# Revit family: Переходник с наружной резьбой
name_source: partatom
category: Соединительные детали трубопроводов
revit_build: Autodesk Revit 2017 (Build: 20160225_1515(x64)
units: mm (PartAtom-declared; Revit-internal decimal feet)

## family parameters
Всегда вертикально = Да
На основе рабочей плоскости = Нет
Общий = Нет
При загрузке вырезать с полостями = Нет
Размер круглого соединителя = Использовать радиус
Тип детали = Соединение

## types (12) — shared parameters
ADSK_Единица измерения = шт
ADSK_Завод-изготовитель = Sanext
URL = http://sanext.ru
Изготовитель = Sanext
Материал фитинга = DZR латунь
Разработчик = ООО ПРОРУБИМ
Разработчик (телефон) = +7(495)649-85-43
Разработчик модели (URL) = http://prorubim.com
zero-valued in all types: ADSK_Масса

## per-type parameters (varying)
| type | ADSK_Код изделия | D1 | DN | G | G/2 | G1/2 | R | R1 | S | a | Лево | Право |
| Переходник с наружной резьбой  63xR 2" | 4275 | 68 мм | 63 мм | 63 мм | 32 мм | 33 мм | 32 мм | 29 мм | 68 мм | 106 мм | Нет | Да |
| Переходник с наружной резьбой  50xR1 1/4" | 4263 | 55 мм | 50 мм | 40 мм | 20 мм | 27 мм | 25 мм | 22 мм | 55 мм | 90 мм | Да | Нет |
| Переходник с наружной резьбой  40xR1 1/4" | 4253 | 45 мм | 40 мм | 40 мм | 20 мм | 22 мм | 20 мм | 17 мм | 45 мм | 83 мм | Нет | Да |
| Переходник с наружной резьбой  32xR1" | 4242 | 37 мм | 32 мм | 32 мм | 16 мм | 18 мм | 16 мм | 13 мм | 37 мм | 73 мм | Нет | Да |
| Переходник с наружной резьбой  32xR3/4" | 4241 | 37 мм | 32 мм | 25 мм | 13 мм | 18 мм | 16 мм | 13 мм | 37 мм | 69 мм | Да | Нет |
| Переходник с наружной резьбой  25xR1" | 4232 | 37 мм | 25 мм | 32 мм | 16 мм | 18 мм | 13 мм | 10 мм | 37 мм | 69 мм | Нет | Да |
| Переходник с наружной резьбой  25xR3/4" | 4231 | 30 мм | 25 мм | 25 мм | 13 мм | 14 мм | 13 мм | 10 мм | 30 мм | 68 мм | Нет | Да |
| Переходник с наружной резьбой  20xR3/4" | 4221 | 30 мм | 20 мм | 25 мм | 13 мм | 14 мм | 10 мм | 7 мм | 30 мм | 56 мм | Нет | Да |
| Переходник с наружной резьбой  20xR1/2" | 4220 | 25 мм | 20 мм | 20 мм | 10 мм | 12 мм | 10 мм | 7 мм | 25 мм | 56 мм | Нет | Да |
| Переходник с наружной резьбой  16xR3/4" | 4211 | 30 мм | 16 мм | 25 мм | 13 мм | 14 мм | 8 мм | 5 мм | 30 мм | 50 мм | Нет | Да |
| Переходник с наружной резьбой  16xR1/2" | 4210 | 25 мм | 16 мм | 20 мм | 10 мм | 12 мм | 8 мм | 5 мм | 25 мм | 49 мм | Нет | Да |
| Переходник с наружной резьбой  50xR1 1/2" | 4264 | 55 мм | 50 мм | 50 мм | 25 мм | 27 мм | 25 мм | 22 мм | 55 мм | 90 мм | Нет | Да |

note: column(s) folded — value = type name in every type: ADSK_Наименование
